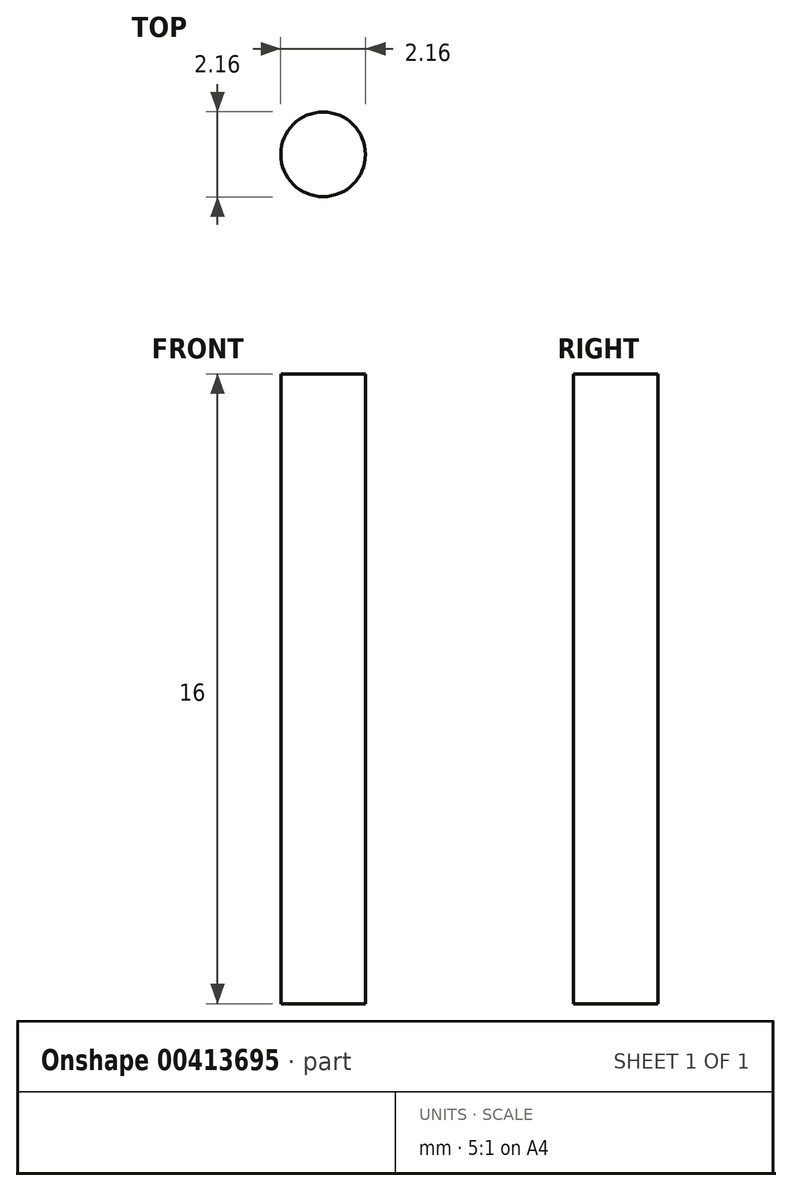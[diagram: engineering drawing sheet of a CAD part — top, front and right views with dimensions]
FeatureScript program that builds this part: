
annotation { "Feature Type Name" : "Feature", "Feature Type Description" : "" }
export const myFeature = defineFeature(function(context is Context, id is Id, definition is map)
    precondition{}
    {
        {
            var Q0;
            Q0=qCreatedBy(makeId("Top.planeOp"),FACE);
            var sketch = newSketch(context, id + "F0", { "sketchPlane" : qUnion([Q0])});
            skCircle(sketch, "E0", {"center": v(0, 0) * mm, "radius": 1.08 * mm});
            skSolve(sketch);
        }
        {
            var Q0;
            Q0=makeQuery(id+"F0.imprint","IMPRINT",FACE,{"disambiguationData":[TD([[makeQuery(id+"F0.imprint","IMPRINT",EDGE,{"derivedFrom":sQuery(id+"F0.wireOp",EDGE,"E0")}),1.0]])]});
            extrude(context, id + "F1", {"entities" : qUnion([Q0]), "depth" : 16 * mm});
        }
    });
